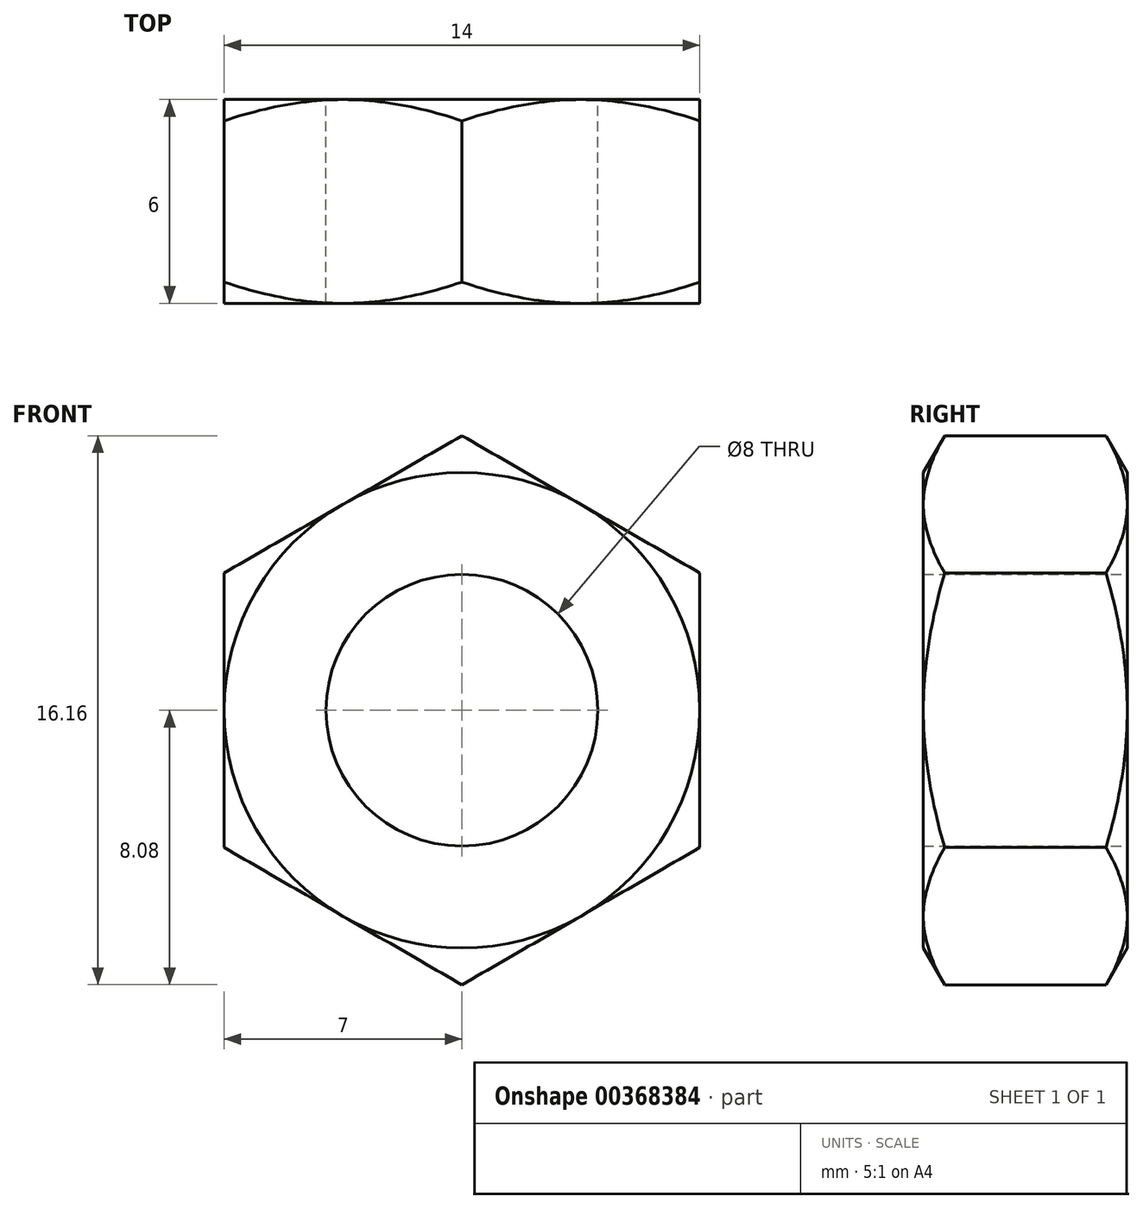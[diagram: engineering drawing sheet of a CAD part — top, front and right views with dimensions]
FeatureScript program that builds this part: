
annotation { "Feature Type Name" : "Feature", "Feature Type Description" : "" }
export const myFeature = defineFeature(function(context is Context, id is Id, definition is map)
    precondition{}
    {
        {
            var Q0;
            Q0=qCreatedBy(makeId("Front.planeOp"),FACE);
            var sketch = newSketch(context, id + "F0", { "sketchPlane" : qUnion([Q0])});
            skCircle(sketch, "E0.cCircle", {"center": v(0, 0) * mm, "radius": 7 * mm, "construction": true});
            skLineSegment(sketch, "E0.0", {"start": v(7, 4.04) * mm, "end": v(7, -4.04) * mm});
            skLineSegment(sketch, "E0.1", {"start": v(7, -4.04) * mm, "end": v(0, -8.08) * mm});
            skLineSegment(sketch, "E0.2", {"start": v(0, -8.08) * mm, "end": v(-7, -4.04) * mm});
            skLineSegment(sketch, "E0.3", {"start": v(-7, -4.04) * mm, "end": v(-7, 4.04) * mm});
            skLineSegment(sketch, "E0.4", {"start": v(-7, 4.04) * mm, "end": v(0, 8.08) * mm});
            skLineSegment(sketch, "E0.5", {"start": v(0, 8.08) * mm, "end": v(7, 4.04) * mm});
            skPoint(sketch, "E0.0.midPoint", {"position": v(7, 0) * mm});
            skCircle(sketch, "E1", {"center": v(0, 0) * mm, "radius": 4 * mm});
            skSolve(sketch);
        }
        {
            var Q0;
            Q0 = qSketchRegion(id + "F0", true);
            extrude(context, id + "F1", {"entities" : qUnion([Q0]), "depth" : 6 * mm});
        }
        {
            var Q0;
            Q0=qCreatedBy(makeId("Top.planeOp"),FACE);
            var sketch = newSketch(context, id + "F2", { "sketchPlane" : qUnion([Q0])});
            skLineSegment(sketch, "E2", {"start": v(0, 0) * mm, "end": v(0, -6) * mm, "construction": true});
            skLineSegment(sketch, "E3", {"start": v(0, -3) * mm, "end": v(7, -3) * mm, "construction": true});
            skPoint(sketch, "E3.endSnap0", {"position": v(0, -3) * mm});
            skLineSegment(sketch, "E4", {"start": v(10.08, 0) * mm, "end": v(10.08, -1.78) * mm});
            skLineSegment(sketch, "E5", {"start": v(10.08, -1.78) * mm, "end": v(7, 0) * mm});
            skLineSegment(sketch, "E6", {"start": v(7, 0) * mm, "end": v(10.08, 0) * mm});
            skLineSegment(sketch, "E7.MirrorCS", {"start": v(7, -6) * mm, "end": v(10.08, -6) * mm});
            skLineSegment(sketch, "E8.MirrorCS", {"start": v(10.08, -4.22) * mm, "end": v(7, -6) * mm});
            skLineSegment(sketch, "E9.MirrorCS", {"start": v(10.08, -6) * mm, "end": v(10.08, -4.22) * mm});
            skSolve(sketch);
        }
        {
            var Q0;
            Q0 = qSketchRegion(id + "F2", true);
            var Q1;
            Q1=sQuery(id+"F2.wireOp",EDGE,"E2");
            revolve(context, id + "F3", {"operationType" : NewBodyOperationType.REMOVE, "entities" : qUnion([Q0]), "axis" : qUnion([Q1]), "revolveType" : RevolveType.FULL, "oppositeDirection" : true});
        }
    });
